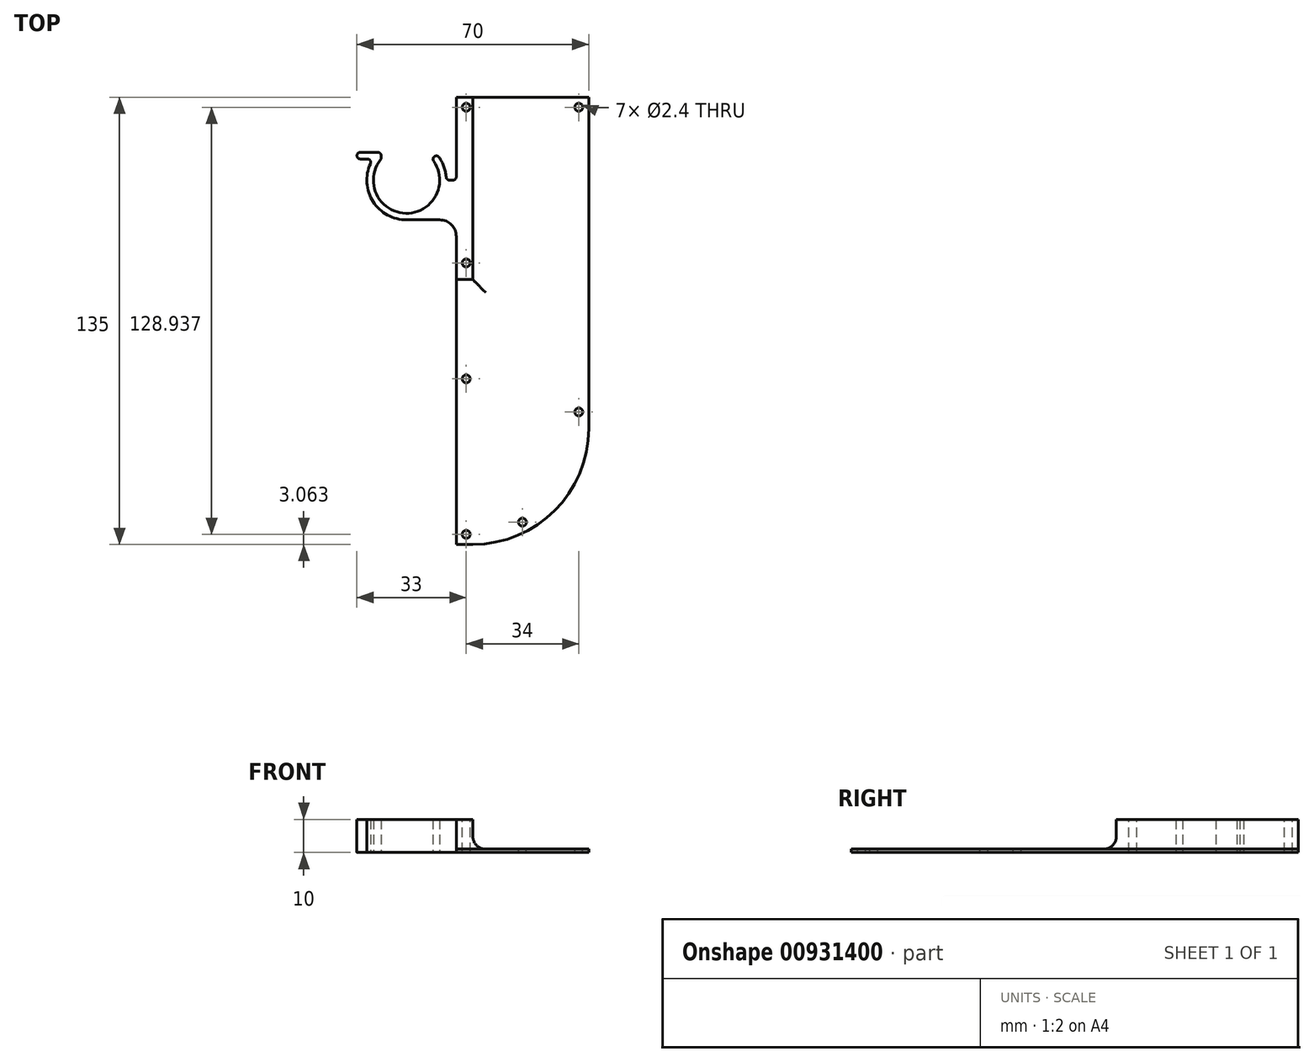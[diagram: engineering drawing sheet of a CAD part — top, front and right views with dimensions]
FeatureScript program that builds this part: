
annotation { "Feature Type Name" : "Feature", "Feature Type Description" : "" }
export const myFeature = defineFeature(function(context is Context, id is Id, definition is map)
    precondition{}
    {
        {
            var Q0;
            Q0=qCreatedBy(makeId("Top.planeOp"),FACE);
            var sketch = newSketch(context, id + "F0", { "sketchPlane" : qUnion([Q0])});
            skLineSegment(sketch, "E0.right", {"start": v(-70, 0) * mm, "end": v(-70, -100) * mm});
            skPoint(sketch, "E1.visualSharp", {"position": v(-70, -135) * mm});
            skArc(sketch, "E1.filletArc", {"start": v(-70, -100) * mm, "mid": v(-59.75, -124.75) * mm, "end": v(-35, -135) * mm});
            skArc(sketch, "E2", {"start": v(-23.18, -19.25) * mm, "mid": v(-14.76, -35) * mm, "end": v(-7.1, -18.86) * mm});
            skPoint(sketch, "E3.visualSharp", {"position": v(-23, -19) * mm});
            skPoint(sketch, "E0.top.start.orphan", {"position": v(0, -135) * mm});
            skPoint(sketch, "E4.visualSharp", {"position": v(-35, -45) * mm});
            skLineSegment(sketch, "E5", {"start": v(-35, -135) * mm, "end": v(-30, -135) * mm});
            skArc(sketch, "E6.0", {"start": v(-15, -37) * mm, "mid": v(-4.9, -31.49) * mm, "end": v(-4.08, -20.02) * mm});
            skLineSegment(sketch, "E7", {"start": v(-30, -135) * mm, "end": v(-30, -42) * mm});
            skLineSegment(sketch, "E8", {"start": v(-25, -37) * mm, "end": v(-15, -37) * mm});
            skPoint(sketch, "E8.endSnap0", {"position": v(-15, -37) * mm});
            skLineSegment(sketch, "E9", {"start": v(-70, 0) * mm, "end": v(-30, 0) * mm});
            skLineSegment(sketch, "E10", {"start": v(-7.18, -17.33) * mm, "end": v(-7.18, -17.33) * mm});
            skPoint(sketch, "E11.visualSharp", {"position": v(-7.86, -18) * mm});
            skPoint(sketch, "E12.visualSharp", {"position": v(-6.43, -16.6) * mm});
            skPoint(sketch, "E13.visualSharp", {"position": v(-30, -37) * mm});
            skArc(sketch, "E13.filletArc", {"start": v(-25, -37) * mm, "mid": v(-28.54, -38.46) * mm, "end": v(-30, -42) * mm});
            skArc(sketch, "E14.0", {"start": v(-24.82, -18.1) * mm, "mid": v(-26.3, -20.94) * mm, "end": v(-26.96, -24.08) * mm});
            skLineSegment(sketch, "E15.top", {"start": v(-27.96, -25) * mm, "end": v(-29, -25) * mm});
            skLineSegment(sketch, "E15.right", {"start": v(-30, 0) * mm, "end": v(-30, -24) * mm});
            skLineSegment(sketch, "E16", {"start": v(-23, -18.68) * mm, "end": v(-23, -18.68) * mm});
            skPoint(sketch, "E15.bottom.start.orphan", {"position": v(-23, 0) * mm});
            skPoint(sketch, "E17.visualSharp", {"position": v(-30, -25) * mm});
            skArc(sketch, "E17.filletArc", {"start": v(-30, -24) * mm, "mid": v(-29.7, -24.7) * mm, "end": v(-29, -25) * mm});
            skArc(sketch, "E18.filletArc", {"start": v(-27.96, -25) * mm, "mid": v(-27.28, -24.73) * mm, "end": v(-26.96, -24.08) * mm});
            skPoint(sketch, "E19.visualSharp", {"position": v(-23, -16.06) * mm});
            skArc(sketch, "E19.filletArc", {"start": v(-23, -18.68) * mm, "mid": v(-23.7, -17.72) * mm, "end": v(-24.82, -18.1) * mm});
            skArc(sketch, "E20.filletArc", {"start": v(-23.18, -19.25) * mm, "mid": v(-23.05, -18.98) * mm, "end": v(-23, -18.68) * mm});
            skLineSegment(sketch, "E21.bottom", {"start": v(-3.17, -18.6) * mm, "end": v(-1, -18.6) * mm});
            skLineSegment(sketch, "E21.top", {"start": v(-6.32, -16.6) * mm, "end": v(-1, -16.6) * mm});
            skLineSegment(sketch, "E21.left", {"start": v(-7.32, -18.25) * mm, "end": v(-7.32, -17.6) * mm});
            skLineSegment(sketch, "E21.right", {"start": v(0, -17.6) * mm, "end": v(0, -17.6) * mm});
            skPoint(sketch, "E22.visualSharp", {"position": v(-7.32, -16.6) * mm});
            skArc(sketch, "E22.filletArc", {"start": v(-6.32, -16.6) * mm, "mid": v(-7.02, -16.9) * mm, "end": v(-7.32, -17.6) * mm});
            skPoint(sketch, "E23.visualSharp", {"position": v(0, -16.6) * mm});
            skArc(sketch, "E23.filletArc", {"start": v(0, -17.6) * mm, "mid": v(-0.3, -16.9) * mm, "end": v(-1, -16.6) * mm});
            skPoint(sketch, "E24.visualSharp", {"position": v(0, -18.6) * mm});
            skArc(sketch, "E24.filletArc", {"start": v(-1, -18.6) * mm, "mid": v(-0.3, -18.3) * mm, "end": v(0, -17.6) * mm});
            skPoint(sketch, "E25.visualSharp", {"position": v(-4.85, -18.6) * mm});
            skArc(sketch, "E25.filletArc", {"start": v(-3.17, -18.6) * mm, "mid": v(-4.02, -19.06) * mm, "end": v(-4.08, -20.02) * mm});
            skPoint(sketch, "E26.visualSharp", {"position": v(-7.32, -18.6) * mm});
            skArc(sketch, "E26.filletArc", {"start": v(-7.32, -18.25) * mm, "mid": v(-7.26, -18.57) * mm, "end": v(-7.1, -18.86) * mm});
            skSolve(sketch);
        }
        {
            var Q0;
            Q0=makeQuery(id+"F0.imprint","IMPRINT",FACE,{"disambiguationData":[TD([[makeQuery(id+"F0.imprint","IMPRINT",EDGE,{"derivedFrom":sQuery(id+"F0.wireOp",EDGE,"E0.right")}),1.0]])]});
            extrude(context, id + "F1", {"entities" : qUnion([Q0]), "depth" : 10 * mm, "offsetDistance" : 25 * mm});
        }
        {
            var Q0;
            Q0=makeQuery(id+"F1.opExtrude","CAP_FACE",FACE,{"disambiguationData":[OSD([sQuery(id+"F0.wireOp",EDGE,"E0.top"),sQuery(id+"F0.wireOp",EDGE,"E0.left"),sQuery(id+"F0.wireOp",EDGE,"E0.right"),sQuery(id+"F0.wireOp",EDGE,"E1.filletArc"),sQuery(id+"F0.wireOp",EDGE,"5de082b1-88c5-4f56-9cd1-09331b00fd2d.trimOffspring"),sQuery(id+"F0.wireOp",EDGE,"E2"),sQuery(id+"F0.wireOp",EDGE,"uJFoRx8a-Ppp5-qDHF-xN9b-6GK6148I28lK.left"),sQuery(id+"F0.wireOp",EDGE,"uJFoRx8a-Ppp5-qDHF-xN9b-6GK6148I28lK.right"),sQuery(id+"F0.wireOp",EDGE,"b2af3c1e-7181-4fb0-8f65-0e7276eb82ca.trimOffspring"),sQuery(id+"F0.wireOp",EDGE,"7f23342a-69af-42d1-8bd4-2c05ba6568f0.filletArc"),sQuery(id+"F0.wireOp",EDGE,"185a892e-41b9-4107-83af-0d2bc894ce6d.filletArc"),sQuery(id+"F0.wireOp",EDGE,"b194760c-3b3b-4794-9b8b-2c71253df791.filletArc"),sQuery(id+"F0.wireOp",EDGE,"E3.filletArc"),sQuery(id+"F0.wireOp",EDGE,"ZXkUyEPo-FX4a-Sv19-M192-gNO29ZRSfF8I"),sQuery(id+"F0.wireOp",EDGE,"HvNRA3BX-9FXn-12fZ-Fs24-gRpAAjMtZzFk")])],"isStart":false});
            var sketch = newSketch(context, id + "F2", { "sketchPlane" : qUnion([Q0])});
            skLineSegment(sketch, "E27", {"start": v(-35, 0) * mm, "end": v(-70, 0) * mm});
            skLineSegment(sketch, "E28", {"start": v(-70, 0) * mm, "end": v(-70, -100) * mm});
            skLineSegment(sketch, "E29", {"start": v(-35, -135) * mm, "end": v(-30, -135) * mm});
            skLineSegment(sketch, "E30", {"start": v(-30, -135) * mm, "end": v(-30, -55) * mm});
            skLineSegment(sketch, "E31", {"start": v(-35, -135) * mm, "end": v(-35, -135) * mm});
            skLineSegment(sketch, "E32", {"start": v(-70, -100) * mm, "end": v(-70, -100) * mm});
            skPoint(sketch, "E33.visualSharp", {"position": v(-70, -135) * mm});
            skArc(sketch, "E33.filletArc", {"start": v(-70, -100) * mm, "mid": v(-59.75, -124.75) * mm, "end": v(-35, -135) * mm});
            skLineSegment(sketch, "E34.top", {"start": v(-30, -55) * mm, "end": v(-35, -55) * mm});
            skLineSegment(sketch, "E34.right", {"start": v(-35, 0) * mm, "end": v(-35, -55) * mm});
            skSolve(sketch);
        }
        {
            var Q0;
            Q0=makeQuery(id+"F2.imprint","IMPRINT",FACE,{"disambiguationData":[TD([[makeQuery(id+"F2.imprint","IMPRINT",EDGE,{"derivedFrom":sQuery(id+"F2.wireOp",EDGE,"ofFXBOQI-h16c-LmGf-cEx5-LxO6o4s5viPL")}),1.0]])]});
            var Q1;
            Q1=makeQuery(id+"F2.imprint","IMPRINT",FACE,{"disambiguationData":[TD([[makeQuery(id+"F2.imprint","IMPRINT",EDGE,{"derivedFrom":sQuery(id+"F2.wireOp",EDGE,"E27")}),-1.0]])]});
            extrude(context, id + "F3", {"entities" : qUnion([Q0, Q1]), "operationType" : NewBodyOperationType.REMOVE, "oppositeDirection" : true, "depth" : 9 * mm, "offsetDistance" : 25 * mm});
        }
        {
            var Q0;
            Q0=makeQuery(id+"F1.opExtrude","CAP_FACE",FACE,{"disambiguationData":[OSD([sQuery(id+"F0.wireOp",EDGE,"E0.top"),sQuery(id+"F0.wireOp",EDGE,"E0.left"),sQuery(id+"F0.wireOp",EDGE,"E0.right"),sQuery(id+"F0.wireOp",EDGE,"E1.filletArc"),sQuery(id+"F0.wireOp",EDGE,"5de082b1-88c5-4f56-9cd1-09331b00fd2d.trimOffspring"),sQuery(id+"F0.wireOp",EDGE,"E2"),sQuery(id+"F0.wireOp",EDGE,"uJFoRx8a-Ppp5-qDHF-xN9b-6GK6148I28lK.left"),sQuery(id+"F0.wireOp",EDGE,"uJFoRx8a-Ppp5-qDHF-xN9b-6GK6148I28lK.right"),sQuery(id+"F0.wireOp",EDGE,"b2af3c1e-7181-4fb0-8f65-0e7276eb82ca.trimOffspring"),sQuery(id+"F0.wireOp",EDGE,"7f23342a-69af-42d1-8bd4-2c05ba6568f0.filletArc"),sQuery(id+"F0.wireOp",EDGE,"185a892e-41b9-4107-83af-0d2bc894ce6d.filletArc"),sQuery(id+"F0.wireOp",EDGE,"b194760c-3b3b-4794-9b8b-2c71253df791.filletArc"),sQuery(id+"F0.wireOp",EDGE,"E3.filletArc"),sQuery(id+"F0.wireOp",EDGE,"ZXkUyEPo-FX4a-Sv19-M192-gNO29ZRSfF8I"),sQuery(id+"F0.wireOp",EDGE,"HvNRA3BX-9FXn-12fZ-Fs24-gRpAAjMtZzFk")])],"isStart":false});
            var sketch = newSketch(context, id + "F4", { "sketchPlane" : qUnion([Q0])});
            skArc(sketch, "E35.1", {"start": v(-67, -100) * mm, "mid": v(-57.63, -122.63) * mm, "end": v(-35, -132) * mm, "construction": true});
            skLineSegment(sketch, "E35.2", {"start": v(-67, 0) * mm, "end": v(-67, -100) * mm, "construction": true});
            skPoint(sketch, "E36", {"position": v(-67, -3) * mm});
            skPoint(sketch, "E37", {"position": v(-50, -128.27) * mm});
            skPoint(sketch, "E38", {"position": v(-33, -131.94) * mm});
            skLineSegment(sketch, "E39.0", {"start": v(-33, 0) * mm, "end": v(-33, -135) * mm, "construction": true});
            skPoint(sketch, "E40", {"position": v(-33, -85) * mm});
            skPoint(sketch, "E41", {"position": v(-33, -50) * mm});
            skPoint(sketch, "E42", {"position": v(-33, -3) * mm});
            skPoint(sketch, "E43", {"position": v(-67, -95) * mm});
            skSolve(sketch);
        }
        {
            var Q0;
            Q0=sQuery(id+"F4.wireOp",VERTEX,"E36");
            var Q1;
            Q1=sQuery(id+"F4.wireOp",VERTEX,"f4559d67-b2ce-4cbe-8c48-f7303b728956.direction1.end");
            var Q2;
            Q2=sQuery(id+"F4.wireOp",VERTEX,"666fff49-049b-4152-8810-0d37dc0279b3");
            var Q3;
            Q3=sQuery(id+"F4.wireOp",VERTEX,"E37");
            var Q4;
            Q4=sQuery(id+"F4.wireOp",VERTEX,"E38");
            var Q5;
            Q5=sQuery(id+"F4.wireOp",VERTEX,"E40");
            var Q6;
            Q6=sQuery(id+"F4.wireOp",VERTEX,"E41");
            var Q7;
            Q7=sQuery(id+"F4.wireOp",VERTEX,"E42");
            var Q8;
            Q8=sQuery(id+"F4.wireOp",VERTEX,"E43");
            var Q9;
            Q9=makeQuery(id+"F1.opExtrude","SWEPT_BODY",BODY,{"disambiguationData":[OSD([sQuery(id+"F0.wireOp",EDGE,"E0.top"),sQuery(id+"F0.wireOp",EDGE,"E0.left"),sQuery(id+"F0.wireOp",EDGE,"E0.right"),sQuery(id+"F0.wireOp",EDGE,"E1.filletArc"),sQuery(id+"F0.wireOp",EDGE,"5de082b1-88c5-4f56-9cd1-09331b00fd2d.trimOffspring"),sQuery(id+"F0.wireOp",EDGE,"E2"),sQuery(id+"F0.wireOp",EDGE,"uJFoRx8a-Ppp5-qDHF-xN9b-6GK6148I28lK.left"),sQuery(id+"F0.wireOp",EDGE,"uJFoRx8a-Ppp5-qDHF-xN9b-6GK6148I28lK.right"),sQuery(id+"F0.wireOp",EDGE,"b2af3c1e-7181-4fb0-8f65-0e7276eb82ca.trimOffspring"),sQuery(id+"F0.wireOp",EDGE,"7f23342a-69af-42d1-8bd4-2c05ba6568f0.filletArc"),sQuery(id+"F0.wireOp",EDGE,"185a892e-41b9-4107-83af-0d2bc894ce6d.filletArc"),sQuery(id+"F0.wireOp",EDGE,"b194760c-3b3b-4794-9b8b-2c71253df791.filletArc"),sQuery(id+"F0.wireOp",EDGE,"E3.filletArc"),sQuery(id+"F0.wireOp",EDGE,"ZXkUyEPo-FX4a-Sv19-M192-gNO29ZRSfF8I"),sQuery(id+"F0.wireOp",EDGE,"HvNRA3BX-9FXn-12fZ-Fs24-gRpAAjMtZzFk")])]});
            hole(context, id + "F5", {"style" : HoleStyle.SIMPLE, "endStyle" : HoleEndStyle.THROUGH, "holeDiameter" : 2.4 * mm, "majorDiameter" : 5 * mm, "isTappedThrough" : true, "tappedDepth" : 12 * mm, "tapClearance" : 3, "locations" : qUnion([Q0, Q1, Q2, Q3, Q4, Q5, Q6, Q7, Q8]), "scope" : qUnion([Q9])});
        }
        {
            var Q0;
            Q0=makeQuery(id+"F3.boolean.opBoolean","COPY",EDGE,{"derivedFrom":makeQuery(id+"F3.opExtrude","CAP_EDGE",EDGE,{"disambiguationData":[OSD([sQuery(id+"F2.wireOp",EDGE,"E34.right")])],"isStart":false})});
            var Q1;
            Q1=makeQuery(id+"F3.boolean.opBoolean","COPY",EDGE,{"derivedFrom":makeQuery(id+"F3.opExtrude","CAP_EDGE",EDGE,{"disambiguationData":[OSD([sQuery(id+"F2.wireOp",EDGE,"E34.top")])],"isStart":false})});
            var Q2;
            Q2=makeQuery(id+"F3.boolean.opBoolean","COPY",EDGE,{"derivedFrom":makeQuery(id+"F3.opExtrude","CAP_EDGE",EDGE,{"disambiguationData":[OSD([sQuery(id+"F2.wireOp",EDGE,"E34.top")])],"isStart":true})});
            var Q3;
            Q3=makeQuery(id+"F3.boolean.opBoolean","COPY",EDGE,{"derivedFrom":makeQuery(id+"F3.opExtrude","CAP_EDGE",EDGE,{"disambiguationData":[OSD([sQuery(id+"F2.wireOp",EDGE,"E34.right")])],"isStart":true})});
            fillet(context, id + "F6", {"entities" : qUnion([Q0, Q1, Q2, Q3]), "radius" : 3.9 * mm, "tangentPropagation" : true, "allowEdgeOverflow" : false});
        }
        {
            var Q0;
            Q0=makeQuery(id+"F1.opExtrude","SWEPT_BODY",BODY,{"disambiguationData":[OSD([sQuery(id+"F0.wireOp",EDGE,"E0.right"),sQuery(id+"F0.wireOp",EDGE,"E1.filletArc"),sQuery(id+"F0.wireOp",EDGE,"E2"),sQuery(id+"F0.wireOp",EDGE,"E5"),sQuery(id+"F0.wireOp",EDGE,"E6.0"),sQuery(id+"F0.wireOp",EDGE,"E7"),sQuery(id+"F0.wireOp",EDGE,"E8"),sQuery(id+"F0.wireOp",EDGE,"E9"),sQuery(id+"F0.wireOp",EDGE,"E13.filletArc"),sQuery(id+"F0.wireOp",EDGE,"E14.0"),sQuery(id+"F0.wireOp",EDGE,"E15.top"),sQuery(id+"F0.wireOp",EDGE,"E15.right"),sQuery(id+"F0.wireOp",EDGE,"E17.filletArc"),sQuery(id+"F0.wireOp",EDGE,"E18.filletArc"),sQuery(id+"F0.wireOp",EDGE,"E19.filletArc"),sQuery(id+"F0.wireOp",EDGE,"E20.filletArc"),sQuery(id+"F0.wireOp",EDGE,"E21.bottom"),sQuery(id+"F0.wireOp",EDGE,"E21.top"),sQuery(id+"F0.wireOp",EDGE,"E21.left"),sQuery(id+"F0.wireOp",EDGE,"E22.filletArc"),sQuery(id+"F0.wireOp",EDGE,"E23.filletArc"),sQuery(id+"F0.wireOp",EDGE,"E24.filletArc"),sQuery(id+"F0.wireOp",EDGE,"E25.filletArc"),sQuery(id+"F0.wireOp",EDGE,"E26.filletArc")])]});
            var Q1;
            Q1=qCreatedBy(makeId("Right.planeOp"),FACE);
            mirror(context, id + "F7", {"operationType" : NewBodyOperationType.ADD, "entities" : qUnion([Q0]), "mirrorPlane" : qUnion([Q1])});
        }
        {
            var Q0;
            Q0=makeQuery(id+"F1.opExtrude","SWEPT_BODY",BODY,{"disambiguationData":[OSD([sQuery(id+"F0.wireOp",EDGE,"E0.right"),sQuery(id+"F0.wireOp",EDGE,"E1.filletArc"),sQuery(id+"F0.wireOp",EDGE,"E2"),sQuery(id+"F0.wireOp",EDGE,"E5"),sQuery(id+"F0.wireOp",EDGE,"E6.0"),sQuery(id+"F0.wireOp",EDGE,"E7"),sQuery(id+"F0.wireOp",EDGE,"E8"),sQuery(id+"F0.wireOp",EDGE,"E9"),sQuery(id+"F0.wireOp",EDGE,"E13.filletArc"),sQuery(id+"F0.wireOp",EDGE,"E14.0"),sQuery(id+"F0.wireOp",EDGE,"E15.top"),sQuery(id+"F0.wireOp",EDGE,"E15.right"),sQuery(id+"F0.wireOp",EDGE,"E17.filletArc"),sQuery(id+"F0.wireOp",EDGE,"E18.filletArc"),sQuery(id+"F0.wireOp",EDGE,"E19.filletArc"),sQuery(id+"F0.wireOp",EDGE,"E20.filletArc"),sQuery(id+"F0.wireOp",EDGE,"E21.bottom"),sQuery(id+"F0.wireOp",EDGE,"E21.top"),sQuery(id+"F0.wireOp",EDGE,"E21.left"),sQuery(id+"F0.wireOp",EDGE,"E22.filletArc"),sQuery(id+"F0.wireOp",EDGE,"E23.filletArc"),sQuery(id+"F0.wireOp",EDGE,"E24.filletArc"),sQuery(id+"F0.wireOp",EDGE,"E25.filletArc"),sQuery(id+"F0.wireOp",EDGE,"E26.filletArc")])]});
            deleteBodies(context, id + "F8", {"entities" : qUnion([Q0])});
        }
    });
